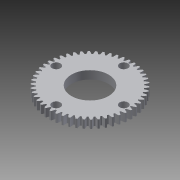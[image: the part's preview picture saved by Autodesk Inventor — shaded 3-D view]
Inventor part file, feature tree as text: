
AUTODESK INVENTOR PART (.ipt)
format: ipt  version: 2013 (Build 170138000, 138)  size: 428,544 bytes
history: native  units: in
note: dims shown in document units (in); Inventor stores cm internally (conversion verified against a paired STEP export)
features: extrude x1, sketch x1
ambient origin geometry x8: Origin, YZ Plane, XZ Plane, XY Plane, X Axis, Y Axis, Z Axis, Center Point
bodies: Solid1 (feature_tree)
feature tree (2):
  extrude  "Extrusion1"  Depth=0.26in
  sketch  "Sketch1"  dims[d1=2.09in d2=0.26in d3=0.26in d4=0.26in d5=0.26in d6=1.15in d7=0.25in d8=0.0in]
